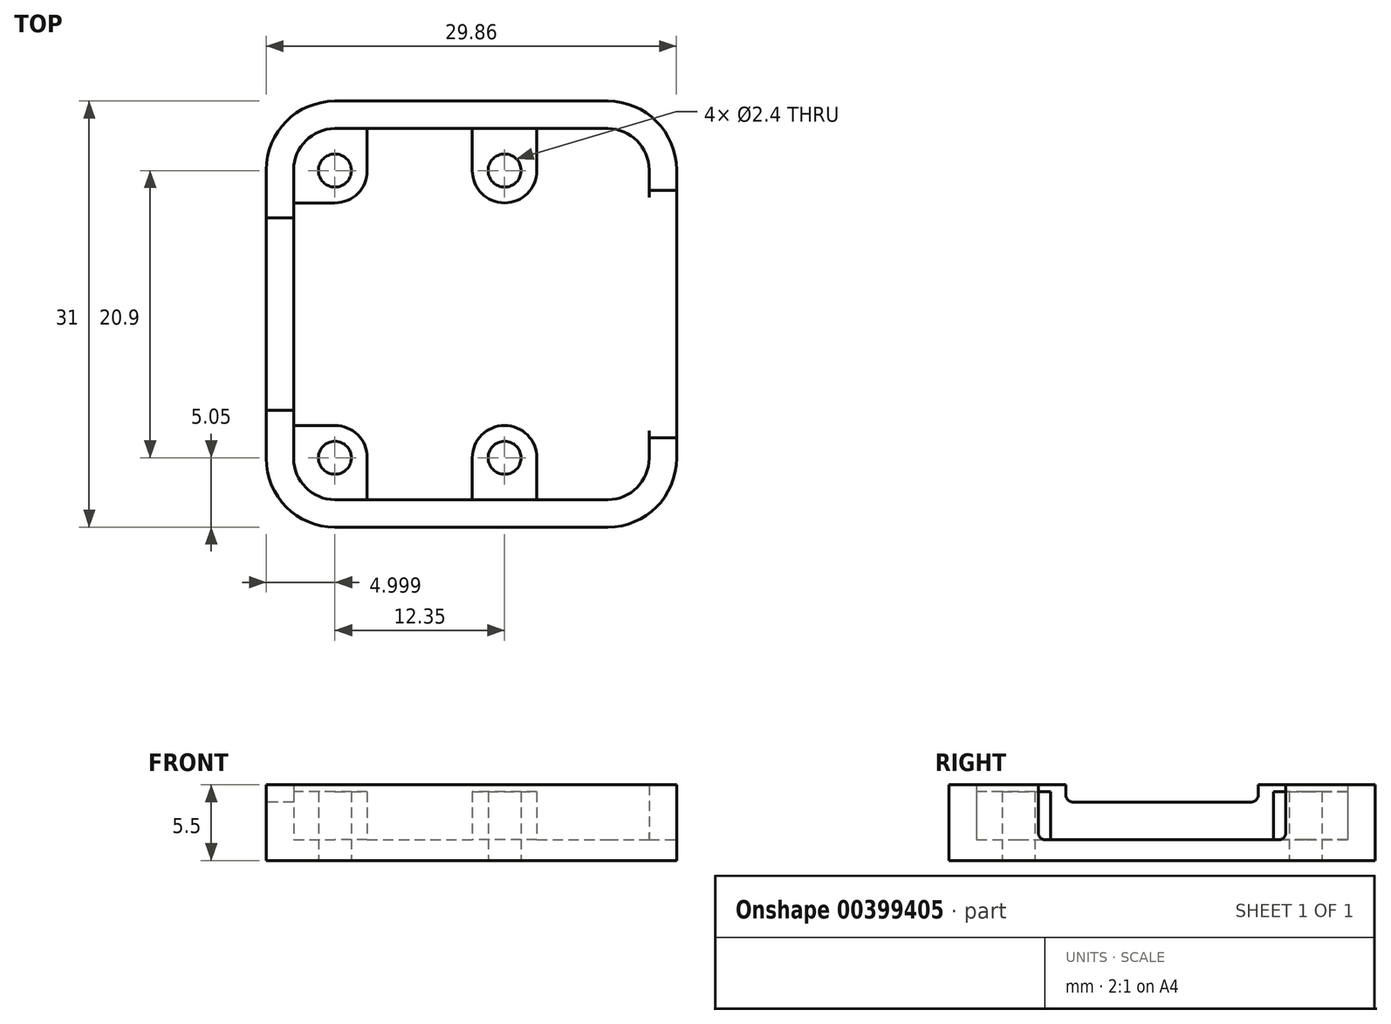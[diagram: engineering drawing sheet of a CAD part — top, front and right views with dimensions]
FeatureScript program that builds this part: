
annotation { "Feature Type Name" : "Feature", "Feature Type Description" : "" }
export const myFeature = defineFeature(function(context is Context, id is Id, definition is map)
    precondition{}
    {
        {
            var Q0;
            Q0=qCreatedBy(makeId("Top.planeOp"),FACE);
            var sketch = newSketch(context, id + "F0", { "sketchPlane" : qUnion([Q0])});
            skPoint(sketch, "E0.middle", {"position": v(0, 0) * mm});
            skPoint(sketch, "E1.visualSharp", {"position": v(-11.93, 12.5) * mm});
            skPoint(sketch, "E2.visualSharp", {"position": v(-11.93, -12.5) * mm});
            skPoint(sketch, "E3.visualSharp", {"position": v(11.93, 12.5) * mm});
            skPoint(sketch, "E4.visualSharp", {"position": v(11.93, -12.5) * mm});
            skLineSegment(sketch, "E5", {"start": v(-9.93, 14.98) * mm, "end": v(-9.93, -15.05) * mm, "construction": true});
            skLineSegment(sketch, "E6", {"start": v(-20.4, -10.45) * mm, "end": v(21.47, -10.45) * mm, "construction": true});
            skLineSegment(sketch, "E7", {"start": v(-14.71, 10.45) * mm, "end": v(19.25, 10.45) * mm, "construction": true});
            skCircle(sketch, "E8", {"center": v(-9.93, 10.45) * mm, "radius": 1.2 * mm});
            skCircle(sketch, "E9", {"center": v(-9.93, -10.45) * mm, "radius": 1.2 * mm});
            skLineSegment(sketch, "E10", {"start": v(2.42, 14.76) * mm, "end": v(2.42, -15.1) * mm, "construction": true});
            skCircle(sketch, "E11", {"center": v(2.42, 10.45) * mm, "radius": 1.2 * mm});
            skCircle(sketch, "E12", {"center": v(2.42, -10.45) * mm, "radius": 1.2 * mm});
            skLineSegment(sketch, "E13", {"start": v(2.47, 15.16) * mm, "end": v(2.47, -14.75) * mm, "construction": true});
            skPoint(sketch, "E14.middle", {"position": v(2.47, 0) * mm});
            skCircle(sketch, "E15", {"center": v(-9.93, 10.45) * mm, "radius": 2.35 * mm});
            skCircle(sketch, "E16", {"center": v(-9.93, -10.45) * mm, "radius": 2.35 * mm});
            skCircle(sketch, "E17", {"center": v(2.42, -10.45) * mm, "radius": 2.35 * mm});
            skCircle(sketch, "E18", {"center": v(2.42, 10.45) * mm, "radius": 2.35 * mm});
            skLineSegment(sketch, "E19.0", {"start": v(9.93, 13.5) * mm, "end": v(-9.93, 13.5) * mm});
            skArc(sketch, "E19.1", {"start": v(12.93, 10.5) * mm, "mid": v(12.05, 12.62) * mm, "end": v(9.93, 13.5) * mm});
            skArc(sketch, "E19.2", {"start": v(-9.93, 13.5) * mm, "mid": v(-12.05, 12.62) * mm, "end": v(-12.93, 10.5) * mm});
            skLineSegment(sketch, "E19.3", {"start": v(12.93, 10.5) * mm, "end": v(12.93, -10.5) * mm});
            skLineSegment(sketch, "E19.4", {"start": v(-12.93, 10.5) * mm, "end": v(-12.93, -10.5) * mm});
            skArc(sketch, "E19.5", {"start": v(-12.93, -10.5) * mm, "mid": v(-12.05, -12.62) * mm, "end": v(-9.93, -13.5) * mm});
            skLineSegment(sketch, "E19.6", {"start": v(9.93, -13.5) * mm, "end": v(-9.93, -13.5) * mm});
            skArc(sketch, "E19.7", {"start": v(9.93, -13.5) * mm, "mid": v(12.05, -12.62) * mm, "end": v(12.93, -10.5) * mm});
            skArc(sketch, "E20.0", {"start": v(14.93, 10.5) * mm, "mid": v(13.47, 14.04) * mm, "end": v(9.93, 15.5) * mm});
            skLineSegment(sketch, "E20.1", {"start": v(14.93, 10.5) * mm, "end": v(14.93, -10.5) * mm});
            skLineSegment(sketch, "E20.2", {"start": v(9.93, 15.5) * mm, "end": v(-9.93, 15.5) * mm});
            skArc(sketch, "E20.3", {"start": v(9.93, -15.5) * mm, "mid": v(13.47, -14.04) * mm, "end": v(14.93, -10.5) * mm});
            skArc(sketch, "E20.4", {"start": v(-9.93, 15.5) * mm, "mid": v(-13.47, 14.04) * mm, "end": v(-14.93, 10.5) * mm});
            skLineSegment(sketch, "E20.5", {"start": v(-14.93, 10.5) * mm, "end": v(-14.93, -10.5) * mm});
            skArc(sketch, "E20.6", {"start": v(-14.93, -10.5) * mm, "mid": v(-13.47, -14.04) * mm, "end": v(-9.93, -15.5) * mm});
            skLineSegment(sketch, "E20.7", {"start": v(9.93, -15.5) * mm, "end": v(-9.93, -15.5) * mm});
            skLineSegment(sketch, "E21", {"start": v(-9.93, 8.1) * mm, "end": v(-12.93, 8.1) * mm});
            skLineSegment(sketch, "E22", {"start": v(-7.58, 10.45) * mm, "end": v(-7.58, 13.5) * mm});
            skLineSegment(sketch, "E23", {"start": v(0.07, 10.45) * mm, "end": v(0.07, 13.5) * mm});
            skLineSegment(sketch, "E24", {"start": v(4.77, 10.45) * mm, "end": v(4.77, 13.5) * mm});
            skLineSegment(sketch, "E25", {"start": v(0.07, -10.45) * mm, "end": v(0.07, -13.5) * mm});
            skLineSegment(sketch, "E26", {"start": v(4.77, -10.45) * mm, "end": v(4.77, -13.5) * mm});
            skLineSegment(sketch, "E27", {"start": v(-9.93, -8.1) * mm, "end": v(-12.93, -8.1) * mm});
            skLineSegment(sketch, "E28", {"start": v(-7.58, -10.45) * mm, "end": v(-7.58, -13.5) * mm});
            skSolve(sketch);
        }
        {
            var Q0;
            Q0=makeQuery(id+"F0.imprint","IMPRINT",FACE,{"disambiguationData":[TD([[makeQuery(id+"F0.imprint","IMPRINT",EDGE,{"derivedFrom":sQuery(id+"F0.wireOp",EDGE,"E19.0")}),-1.0]])]});
            var Q1;
            Q1=makeQuery(id+"F0.imprint","IMPRINT",FACE,{"disambiguationData":[TD([[makeQuery(id+"F0.imprint","IMPRINT",EDGE,{"derivedFrom":sQuery(id+"F0.wireOp",EDGE,"E0.left")}),-1.0]])]});
            var Q2;
            Q2=makeQuery(id+"F0.imprint","IMPRINT",FACE,{"disambiguationData":[TD([[makeQuery(id+"F0.imprint","IMPRINT",EDGE,{"derivedFrom":sQuery(id+"F0.wireOp",EDGE,"E12")}),-1.0]])]});
            var Q3;
            {var subQ0=sQuery(id+"F0.wireOp",EDGE,"E2.filletArc");Q3=makeQuery(id+"F0.imprint","IMPRINT",FACE,{"disambiguationData":[TD([[makeQuery(id+"F0.imprint","IMPRINT",EDGE,{"derivedFrom":subQ0}),1.0]])]});}
            var Q4;
            Q4=makeQuery(id+"F0.imprint","IMPRINT",FACE,{"disambiguationData":[TD([[makeQuery(id+"F0.imprint","IMPRINT",EDGE,{"derivedFrom":sQuery(id+"F0.wireOp",EDGE,"E0.left")}),1.0]])]});
            var Q5;
            {var subQ0=sQuery(id+"F0.wireOp",EDGE,"E1.filletArc");Q5=makeQuery(id+"F0.imprint","IMPRINT",FACE,{"disambiguationData":[TD([[makeQuery(id+"F0.imprint","IMPRINT",EDGE,{"derivedFrom":subQ0}),1.0]])]});}
            var Q6;
            Q6=makeQuery(id+"F0.imprint","IMPRINT",FACE,{"disambiguationData":[TD([[makeQuery(id+"F0.imprint","IMPRINT",EDGE,{"derivedFrom":sQuery(id+"F0.wireOp",EDGE,"E11")}),-1.0]])]});
            var Q7;
            {var subQ0=sQuery(id+"F0.wireOp",EDGE,"E18");var subQ1=sQuery(id+"F0.wireOp",EDGE,"E0.bottom");var subQ2=makeQuery(id+"F0.imprint","INTERSECT",VERTEX,{"disambiguationData":[OD(0.0)],"derivedFrom":[subQ1,subQ0]});Q7=makeQuery(id+"F0.imprint","IMPRINT",FACE,{"disambiguationData":[TD([[makeQuery(id+"F0.imprint","IMPRINT",EDGE,{"disambiguationData":[TD([[subQ2,-1.0]])],"derivedFrom":subQ1}),-1.0]])]});}
            var Q8;
            {var subQ0=sQuery(id+"F0.wireOp",EDGE,"E1.filletArc");Q8=makeQuery(id+"F0.imprint","IMPRINT",FACE,{"disambiguationData":[TD([[makeQuery(id+"F0.imprint","IMPRINT",EDGE,{"derivedFrom":subQ0}),-1.0]])]});}
            var Q9;
            {var subQ0=sQuery(id+"F0.wireOp",EDGE,"E2.filletArc");Q9=makeQuery(id+"F0.imprint","IMPRINT",FACE,{"disambiguationData":[TD([[makeQuery(id+"F0.imprint","IMPRINT",EDGE,{"derivedFrom":subQ0}),-1.0]])]});}
            var Q10;
            {var subQ0=sQuery(id+"F0.wireOp",EDGE,"E17");var subQ1=sQuery(id+"F0.wireOp",EDGE,"E0.top");var subQ2=makeQuery(id+"F0.imprint","INTERSECT",VERTEX,{"disambiguationData":[OD(0.0)],"derivedFrom":[subQ1,subQ0]});Q10=makeQuery(id+"F0.imprint","IMPRINT",FACE,{"disambiguationData":[TD([[makeQuery(id+"F0.imprint","IMPRINT",EDGE,{"disambiguationData":[TD([[subQ2,-1.0]])],"derivedFrom":subQ1}),1.0]])]});}
            var Q11;
            {var subQ0=sQuery(id+"F0.wireOp",EDGE,"E19.2");Q11=makeQuery(id+"F0.imprint","IMPRINT",FACE,{"disambiguationData":[TD([[makeQuery(id+"F0.imprint","IMPRINT",EDGE,{"derivedFrom":subQ0}),1.0]])]});}
            var Q12;
            {var subQ0=sQuery(id+"F0.wireOp",EDGE,"E21");var subQ1=sQuery(id+"F0.wireOp",EDGE,"E0.right");var subQ2=makeQuery(id+"F0.imprint","INTERSECT",VERTEX,{"derivedFrom":[subQ1,subQ0]});Q12=makeQuery(id+"F0.imprint","IMPRINT",FACE,{"disambiguationData":[TD([[makeQuery(id+"F0.imprint","IMPRINT",EDGE,{"disambiguationData":[TD([[subQ2,-1.0]])],"derivedFrom":subQ1}),-1.0]])]});}
            var Q13;
            {var subQ0=sQuery(id+"F0.wireOp",EDGE,"E19.5");Q13=makeQuery(id+"F0.imprint","IMPRINT",FACE,{"disambiguationData":[TD([[makeQuery(id+"F0.imprint","IMPRINT",EDGE,{"derivedFrom":subQ0}),1.0]])]});}
            var Q14;
            {var subQ0=sQuery(id+"F0.wireOp",EDGE,"E27");var subQ1=sQuery(id+"F0.wireOp",EDGE,"E0.right");var subQ2=makeQuery(id+"F0.imprint","INTERSECT",VERTEX,{"derivedFrom":[subQ1,subQ0]});Q14=makeQuery(id+"F0.imprint","IMPRINT",FACE,{"disambiguationData":[TD([[makeQuery(id+"F0.imprint","IMPRINT",EDGE,{"disambiguationData":[TD([[subQ2,-1.0]])],"derivedFrom":subQ1}),1.0]])]});}
            var Q15;
            {var subQ0=sQuery(id+"F0.wireOp",EDGE,"E28");var subQ1=sQuery(id+"F0.wireOp",EDGE,"E0.top");var subQ2=makeQuery(id+"F0.imprint","INTERSECT",VERTEX,{"derivedFrom":[subQ1,subQ0]});Q15=makeQuery(id+"F0.imprint","IMPRINT",FACE,{"disambiguationData":[TD([[makeQuery(id+"F0.imprint","IMPRINT",EDGE,{"disambiguationData":[TD([[subQ2,-1.0]])],"derivedFrom":subQ1}),-1.0]])]});}
            var Q16;
            {var subQ0=sQuery(id+"F0.wireOp",EDGE,"E25");var subQ1=sQuery(id+"F0.wireOp",EDGE,"E0.top");var subQ2=makeQuery(id+"F0.imprint","INTERSECT",VERTEX,{"derivedFrom":[subQ1,subQ0]});Q16=makeQuery(id+"F0.imprint","IMPRINT",FACE,{"disambiguationData":[TD([[makeQuery(id+"F0.imprint","IMPRINT",EDGE,{"disambiguationData":[TD([[subQ2,-1.0]])],"derivedFrom":subQ1}),1.0]])]});}
            var Q17;
            {var subQ3=sQuery(id+"F0.wireOp",EDGE,"E26");var subQ6=sQuery(id+"F0.wireOp",EDGE,"E0.top");var subQ10=makeQuery(id+"F0.imprint","INTERSECT",VERTEX,{"derivedFrom":[subQ6,subQ3]});Q17=makeQuery(id+"F0.imprint","IMPRINT",FACE,{"disambiguationData":[TD([[makeQuery(id+"F0.imprint","IMPRINT",EDGE,{"disambiguationData":[TD([[subQ10,-1.0]])],"derivedFrom":subQ6}),1.0]])]});}
            var Q18;
            {var subQ0=sQuery(id+"F0.wireOp",EDGE,"E26");var subQ1=sQuery(id+"F0.wireOp",EDGE,"E0.top");var subQ2=makeQuery(id+"F0.imprint","INTERSECT",VERTEX,{"derivedFrom":[subQ1,subQ0]});Q18=makeQuery(id+"F0.imprint","IMPRINT",FACE,{"disambiguationData":[TD([[makeQuery(id+"F0.imprint","IMPRINT",EDGE,{"disambiguationData":[TD([[subQ2,-1.0]])],"derivedFrom":subQ1}),-1.0]])]});}
            var Q19;
            {var subQ0=sQuery(id+"F0.wireOp",EDGE,"E17");var subQ1=sQuery(id+"F0.wireOp",EDGE,"E0.top");var subQ2=makeQuery(id+"F0.imprint","INTERSECT",VERTEX,{"disambiguationData":[OD(1.0)],"derivedFrom":[subQ1,subQ0]});Q19=makeQuery(id+"F0.imprint","IMPRINT",FACE,{"disambiguationData":[TD([[makeQuery(id+"F0.imprint","IMPRINT",EDGE,{"disambiguationData":[TD([[subQ2,-1.0]])],"derivedFrom":subQ1}),-1.0]])]});}
            var Q20;
            {var subQ0=sQuery(id+"F0.wireOp",EDGE,"E22");var subQ1=sQuery(id+"F0.wireOp",EDGE,"E0.bottom");var subQ2=makeQuery(id+"F0.imprint","INTERSECT",VERTEX,{"derivedFrom":[subQ1,subQ0]});Q20=makeQuery(id+"F0.imprint","IMPRINT",FACE,{"disambiguationData":[TD([[makeQuery(id+"F0.imprint","IMPRINT",EDGE,{"disambiguationData":[TD([[subQ2,-1.0]])],"derivedFrom":subQ1}),1.0]])]});}
            var Q21;
            {var subQ0=sQuery(id+"F0.wireOp",EDGE,"E15");var subQ1=sQuery(id+"F0.wireOp",EDGE,"E0.right");var subQ2=makeQuery(id+"F0.imprint","INTERSECT",VERTEX,{"derivedFrom":[subQ1,subQ0]});Q21=makeQuery(id+"F0.imprint","IMPRINT",FACE,{"disambiguationData":[TD([[makeQuery(id+"F0.imprint","IMPRINT",EDGE,{"disambiguationData":[TD([[subQ2,-1.0]])],"derivedFrom":subQ1}),1.0]])]});}
            var Q22;
            {var subQ0=sQuery(id+"F0.wireOp",EDGE,"E23");var subQ1=sQuery(id+"F0.wireOp",EDGE,"E0.bottom");var subQ2=makeQuery(id+"F0.imprint","INTERSECT",VERTEX,{"derivedFrom":[subQ1,subQ0]});Q22=makeQuery(id+"F0.imprint","IMPRINT",FACE,{"disambiguationData":[TD([[makeQuery(id+"F0.imprint","IMPRINT",EDGE,{"disambiguationData":[TD([[subQ2,-1.0]])],"derivedFrom":subQ1}),-1.0]])]});}
            var Q23;
            {var subQ0=sQuery(id+"F0.wireOp",EDGE,"E18");var subQ1=sQuery(id+"F0.wireOp",EDGE,"E0.bottom");var subQ2=makeQuery(id+"F0.imprint","INTERSECT",VERTEX,{"disambiguationData":[OD(1.0)],"derivedFrom":[subQ1,subQ0]});Q23=makeQuery(id+"F0.imprint","IMPRINT",FACE,{"disambiguationData":[TD([[makeQuery(id+"F0.imprint","IMPRINT",EDGE,{"disambiguationData":[TD([[subQ2,-1.0]])],"derivedFrom":subQ1}),1.0]])]});}
            var Q24;
            {var subQ1=sQuery(id+"F0.wireOp",EDGE,"E0.bottom");var subQ7=sQuery(id+"F0.wireOp",EDGE,"E24");var subQ9=makeQuery(id+"F0.imprint","INTERSECT",VERTEX,{"derivedFrom":[subQ1,subQ7]});Q24=makeQuery(id+"F0.imprint","IMPRINT",FACE,{"disambiguationData":[TD([[makeQuery(id+"F0.imprint","IMPRINT",EDGE,{"disambiguationData":[TD([[subQ9,-1.0]])],"derivedFrom":subQ1}),-1.0]])]});}
            var Q25;
            {var subQ0=sQuery(id+"F0.wireOp",EDGE,"E24");var subQ1=sQuery(id+"F0.wireOp",EDGE,"E0.bottom");var subQ2=makeQuery(id+"F0.imprint","INTERSECT",VERTEX,{"derivedFrom":[subQ1,subQ0]});Q25=makeQuery(id+"F0.imprint","IMPRINT",FACE,{"disambiguationData":[TD([[makeQuery(id+"F0.imprint","IMPRINT",EDGE,{"disambiguationData":[TD([[subQ2,-1.0]])],"derivedFrom":subQ1}),1.0]])]});}
            var Q26;
            Q26=makeQuery(id+"F0.imprint","IMPRINT",FACE,{"disambiguationData":[TD([[makeQuery(id+"F0.imprint","IMPRINT",EDGE,{"derivedFrom":sQuery(id+"F0.wireOp",EDGE,"0e7cc196-94d9-4211-9143-2209eafa79fa.0")}),-1.0]])]});
            var Q27;
            Q27=makeQuery(id+"F0.imprint","IMPRINT",FACE,{"disambiguationData":[TD([[makeQuery(id+"F0.imprint","IMPRINT",EDGE,{"derivedFrom":sQuery(id+"F0.wireOp",EDGE,"E9")}),-1.0]])]});
            var Q28;
            {var subQ0=sQuery(id+"F0.wireOp",EDGE,"E25");Q28=makeQuery(id+"F0.imprint","IMPRINT",FACE,{"disambiguationData":[TD([[makeQuery(id+"F0.imprint","IMPRINT",EDGE,{"derivedFrom":subQ0}),1.0]])]});}
            var Q29;
            Q29=makeQuery(id+"F0.imprint","IMPRINT",FACE,{"disambiguationData":[TD([[makeQuery(id+"F0.imprint","IMPRINT",EDGE,{"derivedFrom":sQuery(id+"F0.wireOp",EDGE,"E8")}),-1.0]])]});
            var Q30;
            {var subQ0=sQuery(id+"F0.wireOp",EDGE,"E23");Q30=makeQuery(id+"F0.imprint","IMPRINT",FACE,{"disambiguationData":[TD([[makeQuery(id+"F0.imprint","IMPRINT",EDGE,{"derivedFrom":subQ0}),-1.0]])]});}
            var Q31;
            {var subQ13=sQuery(id+"F0.wireOp",EDGE,"E19.1");Q31=makeQuery(id+"F0.imprint","IMPRINT",FACE,{"disambiguationData":[TD([[makeQuery(id+"F0.imprint","IMPRINT",EDGE,{"derivedFrom":subQ13}),1.0]])]});}
            extrude(context, id + "F1", {"entities" : qUnion([Q0, Q1, Q2, Q3, Q4, Q5, Q6, Q7, Q8, Q9, Q10, Q11, Q12, Q13, Q14, Q15, Q16, Q17, Q18, Q19, Q20, Q21, Q22, Q23, Q24, Q25, Q26, Q27, Q28, Q29, Q30, Q31]), "depth" : 1.5 * mm});
        }
        {
            var Q0;
            {var subQ1=sQuery(id+"F0.wireOp",EDGE,"E19.2");Q0=makeQuery(id+"F0.imprint","IMPRINT",FACE,{"disambiguationData":[TD([[makeQuery(id+"F0.imprint","IMPRINT",EDGE,{"derivedFrom":subQ1}),1.0]])]});}
            var Q1;
            Q1=makeQuery(id+"F0.imprint","IMPRINT",FACE,{"disambiguationData":[TD([[makeQuery(id+"F0.imprint","IMPRINT",EDGE,{"derivedFrom":sQuery(id+"F0.wireOp",EDGE,"E8")}),-1.0]])]});
            var Q2;
            Q2=makeQuery(id+"F0.imprint","IMPRINT",FACE,{"disambiguationData":[TD([[makeQuery(id+"F0.imprint","IMPRINT",EDGE,{"derivedFrom":sQuery(id+"F0.wireOp",EDGE,"E11")}),-1.0]])]});
            var Q3;
            {var subQ0=sQuery(id+"F0.wireOp",EDGE,"E23");Q3=makeQuery(id+"F0.imprint","IMPRINT",FACE,{"disambiguationData":[TD([[makeQuery(id+"F0.imprint","IMPRINT",EDGE,{"derivedFrom":subQ0}),-1.0]])]});}
            var Q4;
            Q4=makeQuery(id+"F0.imprint","IMPRINT",FACE,{"disambiguationData":[TD([[makeQuery(id+"F0.imprint","IMPRINT",EDGE,{"derivedFrom":sQuery(id+"F0.wireOp",EDGE,"E12")}),-1.0]])]});
            var Q5;
            {var subQ0=sQuery(id+"F0.wireOp",EDGE,"E25");Q5=makeQuery(id+"F0.imprint","IMPRINT",FACE,{"disambiguationData":[TD([[makeQuery(id+"F0.imprint","IMPRINT",EDGE,{"derivedFrom":subQ0}),1.0]])]});}
            var Q6;
            Q6=makeQuery(id+"F0.imprint","IMPRINT",FACE,{"disambiguationData":[TD([[makeQuery(id+"F0.imprint","IMPRINT",EDGE,{"derivedFrom":sQuery(id+"F0.wireOp",EDGE,"E9")}),-1.0]])]});
            var Q7;
            {var subQ1=sQuery(id+"F0.wireOp",EDGE,"E19.5");Q7=makeQuery(id+"F0.imprint","IMPRINT",FACE,{"disambiguationData":[TD([[makeQuery(id+"F0.imprint","IMPRINT",EDGE,{"derivedFrom":subQ1}),1.0]])]});}
            extrude(context, id + "F2", {"entities" : qUnion([Q0, Q1, Q2, Q3, Q4, Q5, Q6, Q7]), "operationType" : NewBodyOperationType.ADD, "depth" : 5 * mm});
        }
        {
            var Q0;
            {var subQ12=sQuery(id+"F0.wireOp",EDGE,"E19.1");Q0=makeQuery(id+"F0.imprint","IMPRINT",FACE,{"disambiguationData":[TD([[makeQuery(id+"F0.imprint","IMPRINT",EDGE,{"derivedFrom":subQ12}),-1.0]])]});}
            extrude(context, id + "F3", {"entities" : qUnion([Q0]), "operationType" : NewBodyOperationType.ADD, "depth" : 5.5 * mm});
        }
        {
            var Q0;
            {var subQ0=sQuery(id+"F0.wireOp",EDGE,"E20.5");Q0=makeQuery(id+"F3.boolean.opBoolean","MERGE",FACE,{"derivedFrom":[makeQuery(id+"F1.opExtrude","SWEPT_FACE",FACE,{"disambiguationData":[OSD([subQ0])]}),makeQuery(id+"F3.opExtrude","SWEPT_FACE",FACE,{"disambiguationData":[OSD([subQ0])]})]});}
            var sketch = newSketch(context, id + "F4", { "sketchPlane" : qUnion([Q0])});
            skLineSegment(sketch, "E29.bottom", {"start": v(-7, 5.5) * mm, "end": v(7, 5.5) * mm});
            skLineSegment(sketch, "E29.top", {"start": v(-6.5, 4.25) * mm, "end": v(6.5, 4.25) * mm});
            skLineSegment(sketch, "E29.left", {"start": v(-7, 5.5) * mm, "end": v(-7, 4.75) * mm});
            skLineSegment(sketch, "E29.right", {"start": v(7, 5.5) * mm, "end": v(7, 4.75) * mm});
            skPoint(sketch, "E30.visualSharp", {"position": v(-7, 4.25) * mm});
            skArc(sketch, "E30.filletArc", {"start": v(-7, 4.75) * mm, "mid": v(-6.85, 4.4) * mm, "end": v(-6.5, 4.25) * mm});
            skPoint(sketch, "E31.visualSharp", {"position": v(7, 4.25) * mm});
            skArc(sketch, "E31.filletArc", {"start": v(6.5, 4.25) * mm, "mid": v(6.85, 4.4) * mm, "end": v(7, 4.75) * mm});
            skSolve(sketch);
        }
        {
            var Q0;
            Q0=makeQuery(id+"F4.imprint","IMPRINT",FACE,{"disambiguationData":[TD([[makeQuery(id+"F4.imprint","IMPRINT",EDGE,{"derivedFrom":sQuery(id+"F4.wireOp",EDGE,"E29.bottom")}),-1.0]])]});
            extrude(context, id + "F5", {"entities" : qUnion([Q0]), "operationType" : NewBodyOperationType.REMOVE, "oppositeDirection" : true, "depth" : 2 * mm});
        }
        {
            var Q0;
            {var subQ0=sQuery(id+"F0.wireOp",EDGE,"E20.1");Q0=makeQuery(id+"F3.boolean.opBoolean","MERGE",FACE,{"derivedFrom":[makeQuery(id+"F1.opExtrude","SWEPT_FACE",FACE,{"disambiguationData":[OSD([subQ0])]}),makeQuery(id+"F3.opExtrude","SWEPT_FACE",FACE,{"disambiguationData":[OSD([subQ0])]})]});}
            var sketch = newSketch(context, id + "F6", { "sketchPlane" : qUnion([Q0])});
            skLineSegment(sketch, "E32.bottom", {"start": v(9, 5.5) * mm, "end": v(-9, 5.5) * mm});
            skLineSegment(sketch, "E32.top", {"start": v(8.5, 1.5) * mm, "end": v(-8.5, 1.5) * mm});
            skLineSegment(sketch, "E32.left", {"start": v(9, 5.5) * mm, "end": v(9, 2) * mm});
            skLineSegment(sketch, "E32.right", {"start": v(-9, 5.5) * mm, "end": v(-9, 2) * mm});
            skPoint(sketch, "E32.middle", {"position": v(0, 3.5) * mm});
            skPoint(sketch, "E33.visualSharp", {"position": v(-9, 1.5) * mm});
            skArc(sketch, "E33.filletArc", {"start": v(-9, 2) * mm, "mid": v(-8.85, 1.65) * mm, "end": v(-8.5, 1.5) * mm});
            skPoint(sketch, "E34.visualSharp", {"position": v(9, 1.5) * mm});
            skArc(sketch, "E34.filletArc", {"start": v(8.5, 1.5) * mm, "mid": v(8.85, 1.65) * mm, "end": v(9, 2) * mm});
            skSolve(sketch);
        }
        {
            var Q0;
            Q0=makeQuery(id+"F6.imprint","IMPRINT",FACE,{"disambiguationData":[TD([[makeQuery(id+"F6.imprint","IMPRINT",EDGE,{"derivedFrom":sQuery(id+"F6.wireOp",EDGE,"E32.bottom")}),1.0]])]});
            extrude(context, id + "F7", {"entities" : qUnion([Q0]), "operationType" : NewBodyOperationType.REMOVE, "oppositeDirection" : true, "depth" : 2 * mm});
        }
    });
